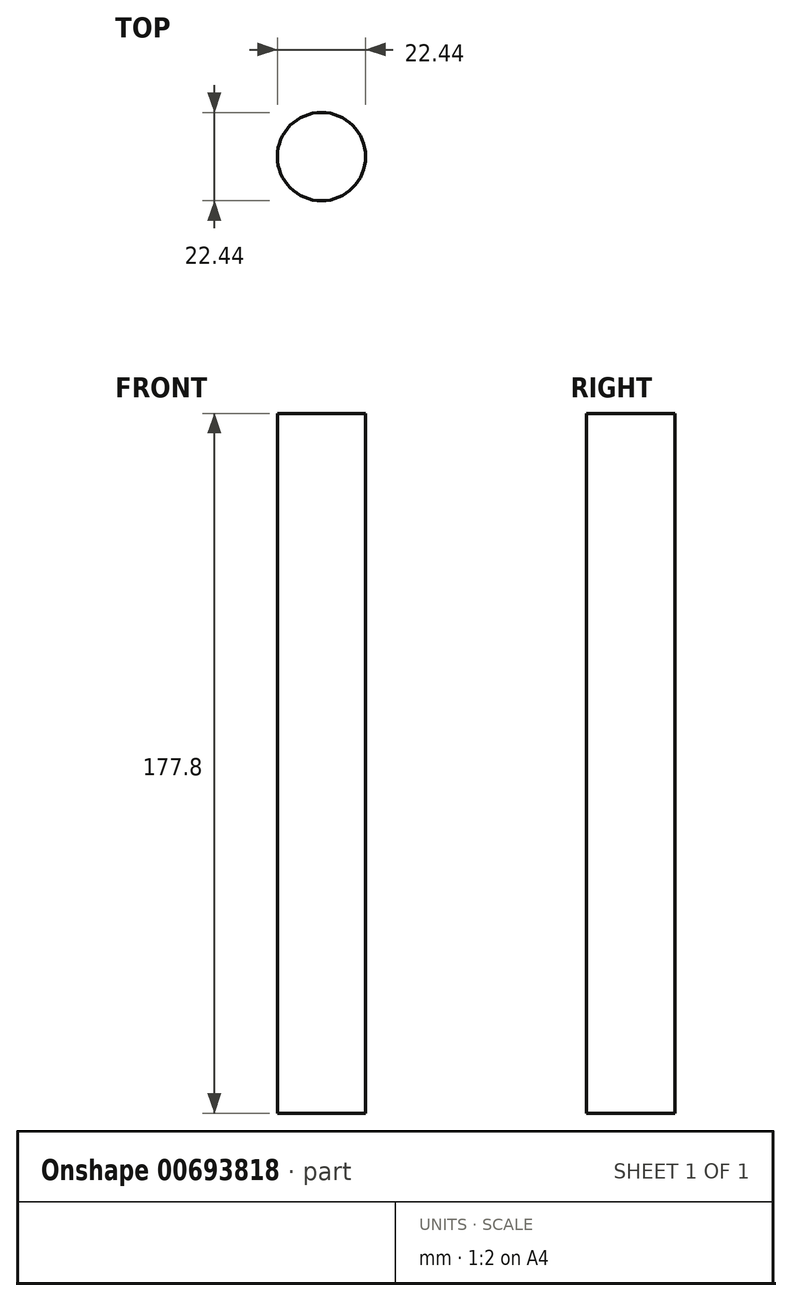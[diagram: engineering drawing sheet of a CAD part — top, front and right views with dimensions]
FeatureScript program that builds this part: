
annotation { "Feature Type Name" : "Feature", "Feature Type Description" : "" }
export const myFeature = defineFeature(function(context is Context, id is Id, definition is map)
    precondition{}
    {
        {
            var Q0;
            Q0=qCreatedBy(makeId("Front.planeOp"),FACE);
            var sketch = newSketch(context, id + "F0", { "sketchPlane" : qUnion([Q0])});
            skLineSegment(sketch, "E0.bottom", {"start": v(-53.15, 13.45) * mm, "end": v(54.73, 13.45) * mm});
            skLineSegment(sketch, "E0.top", {"start": v(-53.15, -12.66) * mm, "end": v(54.73, -12.66) * mm});
            skLineSegment(sketch, "E0.left", {"start": v(-53.15, 13.45) * mm, "end": v(-53.15, -12.66) * mm});
            skLineSegment(sketch, "E0.right", {"start": v(54.73, 13.45) * mm, "end": v(54.73, -12.66) * mm});
            skSolve(sketch);
        }
        {
            var Q0;
            Q0=makeQuery(id+"F0.imprint","IMPRINT",FACE,{"disambiguationData":[TD([[makeQuery(id+"F0.imprint","IMPRINT",EDGE,{"derivedFrom":sQuery(id+"F0.wireOp",EDGE,"E0.bottom")}),-1.0]])]});
            extrude(context, id + "F1", {"entities" : qUnion([Q0]), "depth" : 12.7 * mm, "offsetDistance" : 25.4 * mm});
        }
        {
            var Q0;
            Q0=makeQuery(id+"F1.opExtrude","CAP_FACE",FACE,{"disambiguationData":[OSD([sQuery(id+"F0.wireOp",EDGE,"E0.bottom"),sQuery(id+"F0.wireOp",EDGE,"E0.top"),sQuery(id+"F0.wireOp",EDGE,"E0.left"),sQuery(id+"F0.wireOp",EDGE,"E0.right")])],"isStart":true});
            extrude(context, id + "F2", {"entities" : qUnion([Q0]), "operationType" : NewBodyOperationType.ADD, "depth" : 12.7 * mm, "offsetDistance" : 25.4 * mm});
        }
        {
            var Q0;
            {var subQ0=sQuery(id+"F0.wireOp",EDGE,"E0.top");Q0=makeQuery(id+"F2.boolean.opBoolean","MERGE",FACE,{"derivedFrom":[makeQuery(id+"F1.opExtrude","SWEPT_FACE",FACE,{"disambiguationData":[OSD([subQ0])]}),makeQuery(id+"F2.opExtrude","SWEPT_FACE",FACE,{"disambiguationData":[OSD([subQ0])]})]});}
            var sketch = newSketch(context, id + "F3", { "sketchPlane" : qUnion([Q0])});
            skCircle(sketch, "E1", {"center": v(0, 0) * mm, "radius": 11.22 * mm});
            skSolve(sketch);
        }
        {
            var Q0;
            Q0=makeQuery(id+"F3.imprint","IMPRINT",FACE,{"disambiguationData":[TD([[makeQuery(id+"F3.imprint","IMPRINT",EDGE,{"derivedFrom":sQuery(id+"F3.wireOp",EDGE,"E1")}),1.0]])]});
            extrude(context, id + "F4", {"entities" : qUnion([Q0]), "operationType" : NewBodyOperationType.ADD, "depth" : 177.8 * mm, "offsetDistance" : 25.4 * mm});
        }
        {
            var Q0;
            Q0=makeQuery(id+"F1.opExtrude","CAP_FACE",FACE,{"disambiguationData":[OSD([sQuery(id+"F0.wireOp",EDGE,"E0.bottom"),sQuery(id+"F0.wireOp",EDGE,"E0.top"),sQuery(id+"F0.wireOp",EDGE,"E0.left"),sQuery(id+"F0.wireOp",EDGE,"E0.right")])],"isStart":false});
            extrude(context, id + "F5", {"entities" : qUnion([Q0]), "operationType" : NewBodyOperationType.REMOVE, "oppositeDirection" : true, "depth" : 25.4 * mm, "offsetDistance" : 25.4 * mm});
        }
    });
